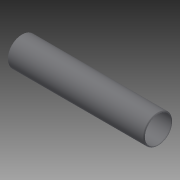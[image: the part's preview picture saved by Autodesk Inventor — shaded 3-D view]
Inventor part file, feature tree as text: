
AUTODESK INVENTOR PART (.ipt)
format: ipt  version: 2014 (Build 180170000, 170)  size: 142,336 bytes
history: native  units: in
note: dims shown in document units (in); Inventor stores cm internally (conversion verified against a paired STEP export)
features: other x42, revolve x1, sketch x1
ambient origin geometry x8: Origin, YZ Plane, XZ Plane, XY Plane, X Axis, Y Axis, Z Axis, Center Point
bodies: Solid1 (feature_tree)
feature tree (44):
  revolve  "Revolution1"  [1 undecoded]
  other  "cp1_XY"
  other  "cp1_YZ"
  other  "cp1_ZX"
  other  "cp1_X"
  other  "cp1_Y"
  other  "cp1_Z"
  other  "cp1_Center"
  other  "cp2_XY"
  other  "cp2_YZ"
  other  "cp2_ZX"
  other  "cp2_X"
  other  "cp2_Y"
  other  "cp2_Z"
  other  "cp2_Center"
  other  "cp3_XY"
  other  "cp3_YZ"
  other  "cp3_ZX"
  other  "cp3_X"
  other  "cp3_Y"
  other  "cp3_Z"
  other  "cp3_Center"
  other  "cp4_XY"
  other  "cp4_YZ"
  other  "cp4_ZX"
  other  "cp4_X"
  other  "cp4_Y"
  other  "cp4_Z"
  other  "cp4_Center"
  other  "tube_front_XY"
  other  "tube_front_YZ"
  other  "tube_front_ZX"
  other  "tube_front_X"
  other  "tube_front_Y"
  other  "tube_front_Z"
  other  "tube_front_Center"
  other  "tube_rear_XY"
  other  "tube_rear_YZ"
  other  "tube_rear_ZX"
  other  "tube_rear_X"
  other  "tube_rear_Y"
  other  "tube_rear_Z"
  other  "tube_rear_Center"
  sketch  "Sketch_1"  dims[d0=360.0deg]
note: 1 required parameter value undecoded (feature->parameter linkage not recoverable at this tier; creation-order binding heuristic only, values carry confidence <= 0.55)
